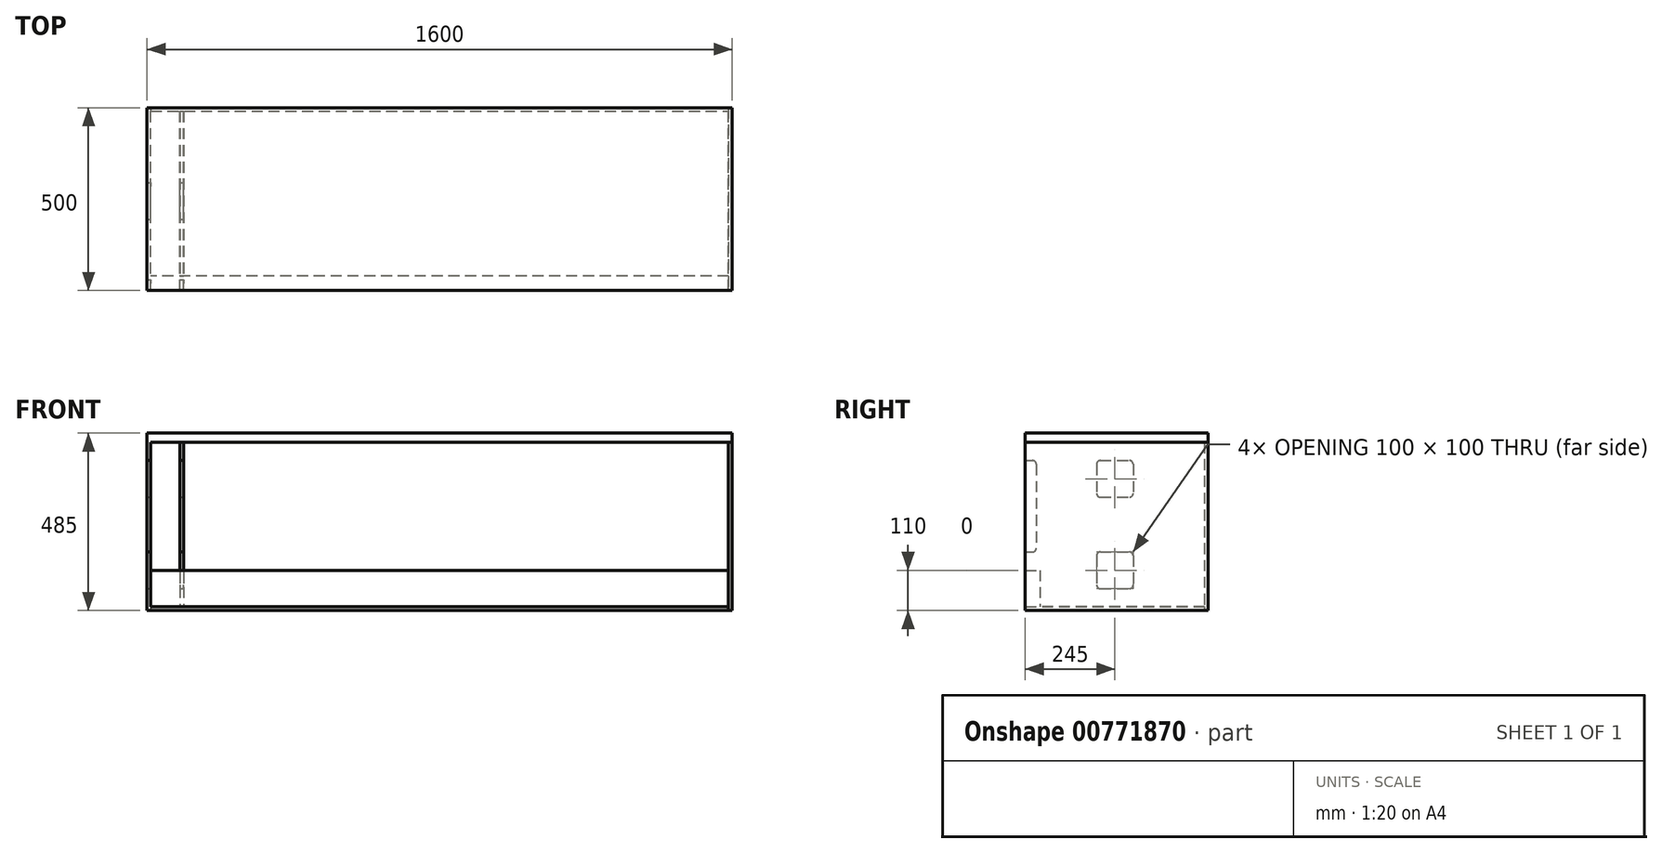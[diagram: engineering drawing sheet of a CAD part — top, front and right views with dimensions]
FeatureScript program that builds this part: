
annotation { "Feature Type Name" : "Feature", "Feature Type Description" : "" }
export const myFeature = defineFeature(function(context is Context, id is Id, definition is map)
    precondition{}
    {
        {
            var Q0;
            Q0=qCreatedBy(makeId("Top.planeOp"),FACE);
            var sketch = newSketch(context, id + "F0", { "sketchPlane" : qUnion([Q0])});
            skLineSegment(sketch, "E0.bottom", {"start": v(0, 0) * mm, "end": v(1600, 0) * mm});
            skLineSegment(sketch, "E0.top", {"start": v(0, 500) * mm, "end": v(1600, 500) * mm});
            skLineSegment(sketch, "E0.left", {"start": v(0, 0) * mm, "end": v(0, 500) * mm});
            skLineSegment(sketch, "E0.right", {"start": v(1600, 0) * mm, "end": v(1600, 500) * mm});
            skSolve(sketch);
        }
        {
            var Q0;
            Q0=makeQuery(id+"F0.imprint","IMPRINT",FACE,{"disambiguationData":[TD([[makeQuery(id+"F0.imprint","IMPRINT",EDGE,{"derivedFrom":sQuery(id+"F0.wireOp",EDGE,"E0.bottom")}),1.0]])]});
            extrude(context, id + "F1", {"entities" : qUnion([Q0]), "depth" : 25 * mm, "offsetDistance" : 25 * mm});
        }
        {
            var Q0;
            Q0=makeQuery(id+"F0.imprint","IMPRINT",FACE,{"disambiguationData":[TD([[makeQuery(id+"F0.imprint","IMPRINT",EDGE,{"derivedFrom":sQuery(id+"F0.wireOp",EDGE,"E0.bottom")}),1.0]])]});
            cPlane(context, id + "F2", {"entities" : qUnion([Q0]), "cplaneType" : CPlaneType.OFFSET, "offset" : 460 * mm, "oppositeDirection" : true, "width" : 150 * mm, "height" : 150 * mm});
        }
        {
            var Q0;
            Q0=qCreatedBy(id+"F2.planeOp",FACE);
            var sketch = newSketch(context, id + "F3", { "sketchPlane" : qUnion([Q0])});
            skLineSegment(sketch, "E1.bottom", {"start": v(10, 0) * mm, "end": v(1590, 0) * mm});
            skLineSegment(sketch, "E1.top", {"start": v(10, 490) * mm, "end": v(1590, 490) * mm});
            skLineSegment(sketch, "E1.left", {"start": v(10, 0) * mm, "end": v(10, 490) * mm});
            skLineSegment(sketch, "E1.right", {"start": v(1590, 0) * mm, "end": v(1590, 490) * mm});
            skSolve(sketch);
        }
        {
            var Q0;
            Q0=makeQuery(id+"F3.imprint","IMPRINT",FACE,{"disambiguationData":[TD([[makeQuery(id+"F3.imprint","IMPRINT",EDGE,{"derivedFrom":sQuery(id+"F3.wireOp",EDGE,"E1.bottom")}),1.0]])]});
            extrude(context, id + "F4", {"entities" : qUnion([Q0]), "depth" : 10 * mm, "offsetDistance" : 25 * mm});
        }
        {
            var Q0;
            Q0=makeQuery(id+"F0.imprint","IMPRINT",FACE,{"disambiguationData":[TD([[makeQuery(id+"F0.imprint","IMPRINT",EDGE,{"derivedFrom":sQuery(id+"F0.wireOp",EDGE,"E0.bottom")}),1.0]])]});
            var sketch = newSketch(context, id + "F5", { "sketchPlane" : qUnion([Q0])});
            skLineSegment(sketch, "E2.bottom", {"start": v(0, 0) * mm, "end": v(10, 0) * mm});
            skLineSegment(sketch, "E2.top", {"start": v(0, 500) * mm, "end": v(10, 500) * mm});
            skLineSegment(sketch, "E2.left", {"start": v(0, 0) * mm, "end": v(0, 500) * mm});
            skLineSegment(sketch, "E2.right", {"start": v(10, 0) * mm, "end": v(10, 500) * mm});
            skSolve(sketch);
        }
        {
            var Q0;
            Q0=qSketchRegion(id+"F5",true);
            var Q1;
            Q1=makeQuery(id+"F4.opExtrude","CAP_FACE",FACE,{"disambiguationData":[OSD([sQuery(id+"F3.wireOp",EDGE,"E1.bottom"),sQuery(id+"F3.wireOp",EDGE,"E1.top"),sQuery(id+"F3.wireOp",EDGE,"E1.left"),sQuery(id+"F3.wireOp",EDGE,"E1.right")])],"isStart":true});
            extrude(context, id + "F6", {"entities" : qUnion([Q0]), "operationType" : NewBodyOperationType.ADD, "endBound" : BoundingType.UP_TO_SURFACE, "oppositeDirection" : true, "depth" : 25 * mm, "endBoundEntityFace" : qUnion([Q1]), "offsetDistance" : 25 * mm});
        }
        {
            var Q0;
            Q0=makeQuery(id+"F0.imprint","IMPRINT",FACE,{"disambiguationData":[TD([[makeQuery(id+"F0.imprint","IMPRINT",EDGE,{"derivedFrom":sQuery(id+"F0.wireOp",EDGE,"E0.bottom")}),1.0]])]});
            var sketch = newSketch(context, id + "F7", { "sketchPlane" : qUnion([Q0])});
            skLineSegment(sketch, "E3.bottom", {"start": v(1600, 0) * mm, "end": v(1590, 0) * mm});
            skLineSegment(sketch, "E3.top", {"start": v(1600, 500) * mm, "end": v(1590, 500) * mm});
            skLineSegment(sketch, "E3.left", {"start": v(1600, 0) * mm, "end": v(1600, 500) * mm});
            skLineSegment(sketch, "E3.right", {"start": v(1590, 0) * mm, "end": v(1590, 500) * mm});
            skSolve(sketch);
        }
        {
            var Q0;
            Q0=makeQuery(id+"F7.imprint","IMPRINT",FACE,{"disambiguationData":[TD([[makeQuery(id+"F7.imprint","IMPRINT",EDGE,{"derivedFrom":sQuery(id+"F7.wireOp",EDGE,"E3.bottom")}),1.0]])]});
            var Q1;
            Q1=makeQuery(id+"F4.opExtrude","CAP_FACE",FACE,{"disambiguationData":[OSD([sQuery(id+"F3.wireOp",EDGE,"E1.bottom"),sQuery(id+"F3.wireOp",EDGE,"E1.top"),sQuery(id+"F3.wireOp",EDGE,"E1.left"),sQuery(id+"F3.wireOp",EDGE,"E1.right")])],"isStart":true});
            extrude(context, id + "F8", {"entities" : qUnion([Q0]), "endBound" : BoundingType.UP_TO_SURFACE, "oppositeDirection" : true, "depth" : 25 * mm, "endBoundEntityFace" : qUnion([Q1]), "offsetDistance" : 25 * mm});
        }
        {
            var Q0;
            Q0=makeQuery(id+"F6.opExtrude","SWEPT_FACE",FACE,{"disambiguationData":[OSD([sQuery(id+"F5.wireOp",EDGE,"E2.right")])]});
            var sketch = newSketch(context, id + "F9", { "sketchPlane" : qUnion([Q0])});
            skLineSegment(sketch, "E4.bottom", {"start": v(0, -350) * mm, "end": v(40, -350) * mm});
            skLineSegment(sketch, "E4.top", {"start": v(0, -450) * mm, "end": v(40, -450) * mm});
            skLineSegment(sketch, "E4.left", {"start": v(0, -350) * mm, "end": v(0, -450) * mm});
            skLineSegment(sketch, "E4.right", {"start": v(40, -350) * mm, "end": v(40, -450) * mm});
            skSolve(sketch);
        }
        {
            var Q0;
            Q0=makeQuery(id+"F9.imprint","IMPRINT",FACE,{"disambiguationData":[TD([[makeQuery(id+"F9.imprint","IMPRINT",EDGE,{"derivedFrom":sQuery(id+"F9.wireOp",EDGE,"E4.bottom")}),-1.0]])]});
            extrude(context, id + "F10", {"entities" : qUnion([Q0]), "endBound" : BoundingType.UP_TO_NEXT, "depth" : 25 * mm, "offsetDistance" : 25 * mm});
        }
        {
            var Q0;
            Q0=makeQuery(id+"F4.opExtrude","CAP_FACE",FACE,{"disambiguationData":[OSD([sQuery(id+"F3.wireOp",EDGE,"E1.bottom"),sQuery(id+"F3.wireOp",EDGE,"E1.top"),sQuery(id+"F3.wireOp",EDGE,"E1.left"),sQuery(id+"F3.wireOp",EDGE,"E1.right")])],"isStart":false});
            var sketch = newSketch(context, id + "F11", { "sketchPlane" : qUnion([Q0])});
            skLineSegment(sketch, "E5.bottom", {"start": v(100, 490) * mm, "end": v(90, 490) * mm});
            skLineSegment(sketch, "E5.top", {"start": v(100, 40) * mm, "end": v(90, 40) * mm});
            skLineSegment(sketch, "E5.left", {"start": v(100, 490) * mm, "end": v(100, 40) * mm});
            skLineSegment(sketch, "E5.right", {"start": v(90, 490) * mm, "end": v(90, 40) * mm});
            skSolve(sketch);
        }
        {
            var Q0;
            Q0=makeQuery(id+"F11.imprint","IMPRINT",FACE,{"disambiguationData":[TD([[makeQuery(id+"F11.imprint","IMPRINT",EDGE,{"derivedFrom":sQuery(id+"F11.wireOp",EDGE,"E5.bottom")}),-1.0]])]});
            extrude(context, id + "F12", {"entities" : qUnion([Q0]), "endBound" : BoundingType.UP_TO_NEXT, "depth" : 25 * mm, "offsetDistance" : 25 * mm});
        }
        {
            var Q0;
            Q0=makeQuery(id+"F12.opExtrude","SWEPT_FACE",FACE,{"disambiguationData":[OSD([sQuery(id+"F11.wireOp",EDGE,"E5.top")])]});
            var sketch = newSketch(context, id + "F13", { "sketchPlane" : qUnion([Q0])});
            skLineSegment(sketch, "E6.bottom", {"start": v(90, 0) * mm, "end": v(100, 0) * mm});
            skLineSegment(sketch, "E6.top", {"start": v(90, -350) * mm, "end": v(100, -350) * mm});
            skLineSegment(sketch, "E6.left", {"start": v(90, 0) * mm, "end": v(90, -350) * mm});
            skLineSegment(sketch, "E6.right", {"start": v(100, 0) * mm, "end": v(100, -350) * mm});
            skSolve(sketch);
        }
        {
            var Q0;
            Q0=makeQuery(id+"F13.imprint","IMPRINT",FACE,{"disambiguationData":[TD([[makeQuery(id+"F13.imprint","IMPRINT",EDGE,{"derivedFrom":sQuery(id+"F13.wireOp",EDGE,"E6.bottom")}),1.0]])]});
            var Q1;
            Q1=makeQuery(id+"F10.opExtrude","SWEPT_FACE",FACE,{"disambiguationData":[OSD([sQuery(id+"F9.wireOp",EDGE,"E4.left")])]});
            extrude(context, id + "F14", {"entities" : qUnion([Q0]), "endBound" : BoundingType.UP_TO_SURFACE, "depth" : 25 * mm, "endBoundEntityFace" : qUnion([Q1]), "offsetDistance" : 25 * mm});
        }
        {
            var Q0;
            Q0=makeQuery(id+"F14.opExtrude","SWEPT_BODY",BODY,{"disambiguationData":[OSD([sQuery(id+"F13.wireOp",EDGE,"E6.bottom"),sQuery(id+"F13.wireOp",EDGE,"E6.top"),sQuery(id+"F13.wireOp",EDGE,"E6.left"),sQuery(id+"F13.wireOp",EDGE,"E6.right")])]});
            var Q1;
            Q1=makeQuery(id+"F12.opExtrude","SWEPT_BODY",BODY,{"disambiguationData":[OSD([sQuery(id+"F11.wireOp",EDGE,"E5.bottom"),sQuery(id+"F11.wireOp",EDGE,"E5.top"),sQuery(id+"F11.wireOp",EDGE,"E5.left"),sQuery(id+"F11.wireOp",EDGE,"E5.right")])]});
            booleanBodies(context, id + "F15", {"operationType" : BooleanOperationType.UNION, "tools" : qUnion([Q0, Q1])});
        }
        {
            var Q0;
            Q0=makeQuery(id+"F15.opBoolean","MERGE",FACE,{"derivedFrom":[makeQuery(id+"F12.opExtrude","SWEPT_FACE",FACE,{"disambiguationData":[OSD([sQuery(id+"F11.wireOp",EDGE,"E5.left")])]}),makeQuery(id+"F14.opExtrude","SWEPT_FACE",FACE,{"disambiguationData":[OSD([sQuery(id+"F13.wireOp",EDGE,"E6.right")])]})]});
            var sketch = newSketch(context, id + "F16", { "sketchPlane" : qUnion([Q0])});
            skLineSegment(sketch, "E7.bottom", {"start": v(0, -50) * mm, "end": v(30, -50) * mm});
            skLineSegment(sketch, "E7.top", {"start": v(0, -300) * mm, "end": v(30, -300) * mm});
            skLineSegment(sketch, "E7.left", {"start": v(0, -50) * mm, "end": v(0, -300) * mm});
            skLineSegment(sketch, "E7.right", {"start": v(30, -50) * mm, "end": v(30, -300) * mm});
            skSolve(sketch);
        }
        {
            var Q0;
            Q0=makeQuery(id+"F16.imprint","IMPRINT",FACE,{"disambiguationData":[TD([[makeQuery(id+"F16.imprint","IMPRINT",EDGE,{"derivedFrom":sQuery(id+"F16.wireOp",EDGE,"E7.bottom")}),-1.0]])]});
            extrude(context, id + "F17", {"entities" : qUnion([Q0]), "operationType" : NewBodyOperationType.REMOVE, "endBound" : BoundingType.THROUGH_ALL, "oppositeDirection" : true, "depth" : 25 * mm, "offsetDistance" : 25 * mm});
        }
        {
            var Q0;
            Q0=makeQuery(id+"F17.boolean.opBoolean","COPY",EDGE,{"derivedFrom":makeQuery(id+"F17.opExtrude","SWEPT_EDGE",EDGE,{"disambiguationData":[OSD([sQuery(id+"F16.wireOp",EDGE,"E7.bottom"),sQuery(id+"F16.wireOp",EDGE,"E7.right")])]})});
            var Q1;
            Q1=makeQuery(id+"F17.boolean.opBoolean","COPY",EDGE,{"derivedFrom":makeQuery(id+"F17.opExtrude","SWEPT_EDGE",EDGE,{"disambiguationData":[OSD([sQuery(id+"F16.wireOp",EDGE,"E7.top"),sQuery(id+"F16.wireOp",EDGE,"E7.right")])]})});
            fillet(context, id + "F18", {"entities" : qUnion([Q0, Q1]), "radius" : 10 * mm, "tangentPropagation" : true, "allowEdgeOverflow" : false});
        }
        {
            var Q0;
            Q0=makeQuery(id+"F15.opBoolean","MERGE",FACE,{"derivedFrom":[makeQuery(id+"F12.opExtrude","SWEPT_FACE",FACE,{"disambiguationData":[OSD([sQuery(id+"F11.wireOp",EDGE,"E5.left")])]}),makeQuery(id+"F14.opExtrude","SWEPT_FACE",FACE,{"disambiguationData":[OSD([sQuery(id+"F13.wireOp",EDGE,"E6.right")])]})]});
            var sketch = newSketch(context, id + "F19", { "sketchPlane" : qUnion([Q0])});
            skLineSegment(sketch, "E8.bottom", {"start": v(205, -300) * mm, "end": v(285, -300) * mm});
            skLineSegment(sketch, "E8.top", {"start": v(205, -400) * mm, "end": v(285, -400) * mm});
            skLineSegment(sketch, "E8.left", {"start": v(195, -310) * mm, "end": v(195, -390) * mm});
            skLineSegment(sketch, "E8.right", {"start": v(295, -310) * mm, "end": v(295, -390) * mm});
            skPoint(sketch, "E9.visualSharp", {"position": v(195, -300) * mm});
            skArc(sketch, "E9.filletArc", {"start": v(205, -300) * mm, "mid": v(197.93, -302.93) * mm, "end": v(195, -310) * mm});
            skPoint(sketch, "E10.visualSharp", {"position": v(295, -300) * mm});
            skArc(sketch, "E10.filletArc", {"start": v(295, -310) * mm, "mid": v(292.07, -302.93) * mm, "end": v(285, -300) * mm});
            skPoint(sketch, "E11.visualSharp", {"position": v(295, -400) * mm});
            skArc(sketch, "E11.filletArc", {"start": v(285, -400) * mm, "mid": v(292.07, -397.07) * mm, "end": v(295, -390) * mm});
            skPoint(sketch, "E12.visualSharp", {"position": v(195, -400) * mm});
            skArc(sketch, "E12.filletArc", {"start": v(195, -390) * mm, "mid": v(197.93, -397.07) * mm, "end": v(205, -400) * mm});
            skLineSegment(sketch, "E13.bottom", {"start": v(205, -50) * mm, "end": v(285, -50) * mm});
            skLineSegment(sketch, "E13.top", {"start": v(205, -150) * mm, "end": v(285, -150) * mm});
            skLineSegment(sketch, "E13.left", {"start": v(195, -60) * mm, "end": v(195, -140) * mm});
            skLineSegment(sketch, "E13.right", {"start": v(295, -60) * mm, "end": v(295, -140) * mm});
            skPoint(sketch, "E14.visualSharp", {"position": v(195, -50) * mm});
            skArc(sketch, "E14.filletArc", {"start": v(205, -50) * mm, "mid": v(197.93, -52.93) * mm, "end": v(195, -60) * mm});
            skPoint(sketch, "E15.visualSharp", {"position": v(295, -50) * mm});
            skArc(sketch, "E15.filletArc", {"start": v(295, -60) * mm, "mid": v(292.07, -52.93) * mm, "end": v(285, -50) * mm});
            skPoint(sketch, "E16.visualSharp", {"position": v(295, -150) * mm});
            skArc(sketch, "E16.filletArc", {"start": v(285, -150) * mm, "mid": v(292.07, -147.07) * mm, "end": v(295, -140) * mm});
            skPoint(sketch, "E17.visualSharp", {"position": v(195, -150) * mm});
            skArc(sketch, "E17.filletArc", {"start": v(195, -140) * mm, "mid": v(197.93, -147.07) * mm, "end": v(205, -150) * mm});
            skSolve(sketch);
        }
        {
            var Q0;
            Q0=makeQuery(id+"F19.imprint","IMPRINT",FACE,{"disambiguationData":[TD([[makeQuery(id+"F19.imprint","IMPRINT",EDGE,{"derivedFrom":sQuery(id+"F19.wireOp",EDGE,"E13.bottom")}),-1.0]])]});
            var Q1;
            Q1=makeQuery(id+"F19.imprint","IMPRINT",FACE,{"disambiguationData":[TD([[makeQuery(id+"F19.imprint","IMPRINT",EDGE,{"derivedFrom":sQuery(id+"F19.wireOp",EDGE,"E8.bottom")}),-1.0]])]});
            extrude(context, id + "F20", {"entities" : qUnion([Q0, Q1]), "operationType" : NewBodyOperationType.REMOVE, "endBound" : BoundingType.THROUGH_ALL, "oppositeDirection" : true, "depth" : 25 * mm, "offsetDistance" : 25 * mm});
        }
    });
